# Revit family: RN 67103 Set di montaggio valvola sotto muro
name_source: partatom
category: Rohrzubehör
units: mm (PartAtom-declared; Revit-internal decimal feet)

## family parameters
Arbeitsebenenbasiert = Nein
Beim Laden mit Abzugskörper schneiden = Nein
Bemaßung runder Anschluss = Durchmesser verwenden
Gemeinsam genutzt = Nein
Immer vertikal = Ja
Teiletyp = Ventil - Zerlegung in

## types (1)
- DN 20
    1.010.00.2 Blattnummer der Richtlinie = 17
    1.010.00.3 Ausgabedatum (Monat) der Richtlinie = 201601
    1.010.00.4 Herstellername = R. Nussbaum AG
    1.010.00.5 Revisionsdatum der Datei = 20190528
    1.010.00.6 Webadresse des Herstellers = http://www.nussbaum.ch
    1.100.00.3 Sortiernummer für Anzeigereihenfolge = 7
    1.100.00.4 Produktbezeichnung = Mess- und Zähleinrichtungen
    1.800.00.3 TGA-Nummer = 0070140000000000000000000000020070000000000000000100000000
    1.810.00.3 Hersteller-Bestellnummer = 67103.05
    1.810.00.4 DATANORM-Nummer = 67103.05
    1.810.00.5 StLB-Nummer = 652.831
    1.810.00.6 GTIN-Nummer = 7612945736772
    1.960/3L.00.8 Link (URL) = https://www.nussbaum.ch
    17.700.00.30 Produktbeschreibung = 67103.05, Rohbauset-Unterputz-Ventil-Garnitur, lange Ausführung, für Messkapsel K
    17.700.00.4 Armaturentyp = 9
    17.700.00.5 Nennweite DN = 20
    17.700.00.6 kvs-Wert [m3/h] = 3.48
    17.700.00.7 Maximale Betriebstemperatur TB [°C] = 90
    17.700.00.8 Maximaler Betriebsdruck (Arbeitsdruck) ps [1.0 · 105 Pa] = 10
    CONNECTOR0_DIAMETER_dX_0r = 20 mm
    CONNECTOR0_dX_00 = 122 mm
    CONNECTOR0_dX_01 = 107 mm
    CONNECTOR0_ref_dX = 107 mm
    CONNECTOR1_DIAMETER_dX_0r = 20 mm
    CONNECTOR1_dX_00 = 106 mm
    CONNECTOR1_dX_01 = 121 mm
    CONNECTOR1_ref_dX = 106 mm
    Connector Visibility = Nein
    EnclosingSpace Visibility = Nein
    Hersteller = R. Nussbauzm AG
    Modell = 67103.05
    R. Nussbaum AG 67103.05 de Visibility = Ja
    Typenkommentare = Set di montaggio valvola sotto muroDN 20
    URL = https://www.nussbaum.ch

## geometry (parser evidence)
native form markers: Sweep x2
no freeform markers — native parametric forms only
